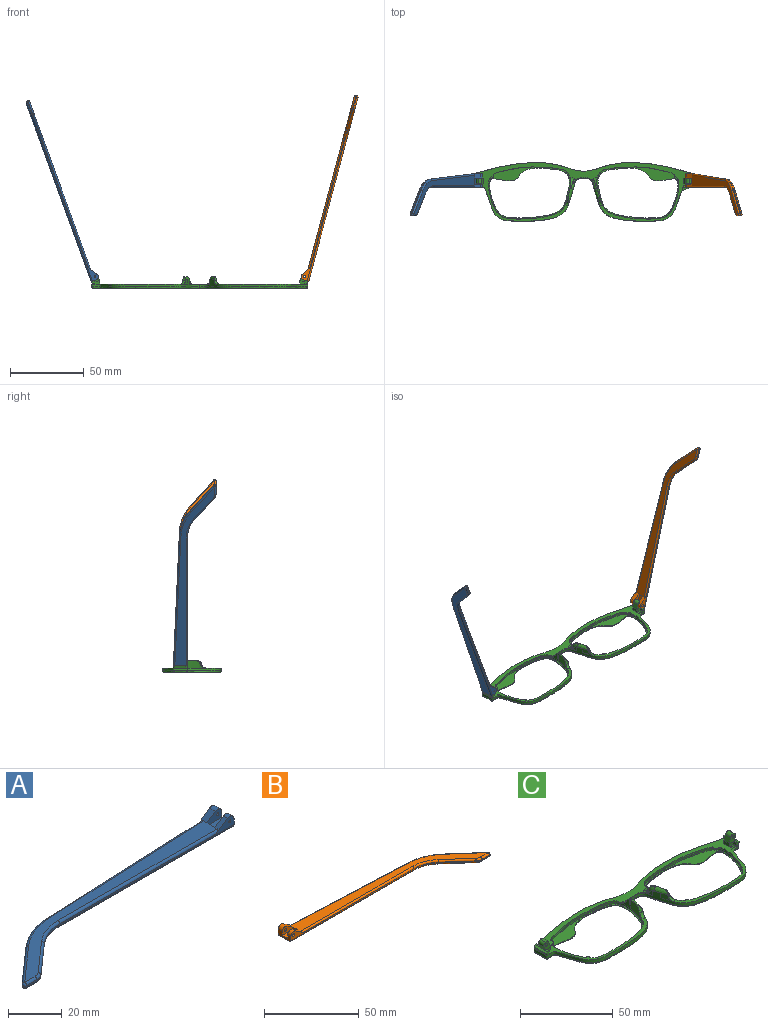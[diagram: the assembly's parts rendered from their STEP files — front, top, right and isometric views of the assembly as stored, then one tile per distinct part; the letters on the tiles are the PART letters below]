
ASSEMBLY  parts=3 mates=2
PART A: 43 faces, bbox 130.2x29.5x5.9 mm
  f0: plane 9.62x3.72mm, normal (1,0,0), area 24.7mm2, adj f1,f3,f4,f5,f10,f16,f18,f28
  f1: cylinder r=2.2mm len=3.45mm, axis (0,-1,0), area 11mm2, adj f0,f2,f4,f37
  f2: plane 6.01x3.91mm, normal (-0.55,0,0.84), area 12.7mm2, adj f1,f4,f9,f19,f37
  f3: plane 2.26x0.1mm, normal (0,0,1), area 0.1mm2, adj f0,f5,f18
  f4: plane 92.1x4.9mm, normal (0,-1,0), area 79.9mm2, adj f0,f1,f2,f14,f19,f36,f42
  f5: plane 93.42x4.13mm, normal (-0.04,1,0), area 64.8mm2, adj f0,f3,f11,f15,f17,f27,f28
  f6: plane 17.82x15.72mm, normal (-0.66,0.75,0), area 14.3mm2, adj f11,f12,f25,f30
  f7: plane 5.46x0.6mm, normal (0,-1,0), area 3.3mm2, adj f12,f13,f23,f32
  f8: plane 14.99x13.23mm, normal (0.66,-0.75,0), area 12mm2, adj f13,f14,f21,f34
  f9: plane 121.18x26.73mm, normal (0,0,1), area 627.7mm2, adj f2,f17,f19,f20,f21,f22,f23,f25
  f10: plane 129.1x27.08mm, normal (0,0,-1), area 686.5mm2, adj f0,f28,f29,f30,f32,f33,f34,f35
  f11: cylinder r=30mm len=18.52mm, axis (0,0,-1), area 12.2mm2, adj f5,f6,f26,f29
  f12: cylinder r=1mm len=1.75mm, axis (0,0,-1), area 1.5mm2, adj f6,f7,f24,f31
  f13: cylinder r=5mm len=3.31mm, axis (0,0,-1), area 2.2mm2, adj f7,f8,f22,f33
  f14: cylinder r=20mm len=13.23mm, axis (0,0,1), area 8.7mm2, adj f4,f8,f20,f35
  f15: plane 5.66x0.25mm, normal (0,0,-1), area 0.7mm2, adj f5,f17,f18
  f16: cylinder r=2.2mm len=3.45mm, axis (0,-1,0), area 14.8mm2, adj f0,f17,f18,f38
  f17: plane 6.01x3.91mm, normal (-0.55,0,0.84), area 16.9mm2, adj f5,f9,f15,f16,f18,f27,f38
  f18: plane 7.92x3.3mm, normal (0,1,0), area 15.9mm2, adj f0,f3,f15,f16,f17,f41
  f19: cylinder r=1mm len=84.18mm, axis (-1,0,0), area 131.4mm2, adj f2,f4,f9,f20
  f20: torus R=21mm, axis (0,0,1), area 23.1mm2, adj f9,f14,f19,f21
  f21: cylinder r=1mm len=15.65mm, axis (-0.75,-0.66,0), area 31.4mm2, adj f8,f9,f20,f22
  f22: torus R=4mm, axis (0,0,1), area 5.3mm2, adj f9,f13,f21,f23
  f23: cylinder r=1mm len=5.46mm, axis (-1,0,0), area 8.6mm2, adj f7,f9,f22,f24
  f24: sphere r=1mm, area 2.4mm2, adj f12,f23,f25
  f25: cylinder r=1mm len=18.48mm, axis (0.75,0.66,0), area 37.3mm2, adj f6,f9,f24,f26
  f26: torus R=29mm, axis (0,0,1), area 31.6mm2, adj f9,f11,f25,f27
  f27: cylinder r=1mm len=85.5mm, axis (1,0.04,0), area 133.5mm2, adj f5,f9,f17,f26
  f28: cylinder r=1mm len=93.46mm, axis (-1,-0.04,0), area 146.9mm2, adj f0,f5,f10,f29
  f29: torus R=29mm, axis (0,0,1), area 31.6mm2, adj f10,f11,f28,f30
  f30: cylinder r=1mm len=18.48mm, axis (-0.75,-0.66,0), area 37.3mm2, adj f6,f10,f29,f31
  f31: sphere r=1mm, area 2.4mm2, adj f12,f30,f32
  f32: cylinder r=1mm len=5.46mm, axis (1,0,0), area 8.6mm2, adj f7,f10,f31,f33
  f33: torus R=4mm, axis (0,0,1), area 5.3mm2, adj f10,f13,f32,f34
  f34: cylinder r=1mm len=15.65mm, axis (0.75,0.66,0), area 31.4mm2, adj f8,f10,f33,f35
  f35: torus R=21mm, axis (0,0,1), area 23.1mm2, adj f10,f14,f34,f36
  f36: cylinder r=1mm len=92.1mm, axis (1,0,0), area 144.7mm2, adj f0,f4,f10,f35
  f37: plane 7.92x4.7mm, normal (0,1,0), area 27mm2, adj f0,f1,f2,f39,f40,f42
  f38: plane 7.92x4.7mm, normal (0,-1,0), area 27mm2, adj f0,f16,f17,f39,f40,f41
  f39: plane 7.92x4.1mm, normal (0,0,1), area 32.5mm2, adj f0,f37,f38,f40
  f40: plane 4.1x1.4mm, normal (1,0,0), area 5.7mm2, adj f9,f37,f38,f39
  f41: cylinder r=0.5mm len=3.1mm, axis (0,-1,0), area 9.7mm2, adj f18,f38
  f42: cylinder r=0.5mm len=2.3mm, axis (0,-1,0), area 7.2mm2, adj f4,f37
PART B: 43 faces, bbox 130.2x29.5x5.9 mm
  f0: plane 9.62x3.72mm, normal (-1,0,0), area 24.7mm2, adj f1,f3,f4,f5,f10,f16,f18,f28
  f1: cylinder r=2.2mm len=3.45mm, axis (0,-1,0), area 11mm2, adj f0,f2,f4,f37
  f2: plane 6.01x3.91mm, normal (0.55,0,0.84), area 12.7mm2, adj f1,f4,f9,f19,f37
  f3: plane 2.26x0.1mm, normal (0,0,1), area 0.1mm2, adj f0,f5,f18
  f4: plane 92.1x4.9mm, normal (0,-1,0), area 78.2mm2, adj f0,f1,f2,f14,f19,f36,f42
  f5: plane 93.42x4.13mm, normal (0.04,1,0), area 64.8mm2, adj f0,f3,f11,f15,f17,f27,f28
  f6: plane 17.82x15.72mm, normal (0.66,0.75,0), area 14.3mm2, adj f11,f12,f25,f30
  f7: plane 5.46x0.6mm, normal (0,-1,0), area 3.3mm2, adj f12,f13,f23,f32
  f8: plane 14.99x13.23mm, normal (-0.66,-0.75,0), area 12mm2, adj f13,f14,f21,f34
  f9: plane 121.18x26.73mm, normal (0,0,1), area 627.7mm2, adj f2,f17,f19,f20,f21,f22,f23,f25
  f10: plane 129.1x27.08mm, normal (0,0,-1), area 686.5mm2, adj f0,f28,f29,f30,f32,f33,f34,f35
  f11: cylinder r=30mm len=18.52mm, axis (0,0,-1), area 12.2mm2, adj f5,f6,f26,f29
  f12: cylinder r=1mm len=1.75mm, axis (0,0,-1), area 1.5mm2, adj f6,f7,f24,f31
  f13: cylinder r=5mm len=3.31mm, axis (0,0,-1), area 2.2mm2, adj f7,f8,f22,f33
  f14: cylinder r=20mm len=13.23mm, axis (0,0,1), area 8.7mm2, adj f4,f8,f20,f35
  f15: plane 5.66x0.25mm, normal (0,0,-1), area 0.7mm2, adj f5,f17,f18
  f16: cylinder r=2.2mm len=3.45mm, axis (0,-1,0), area 14.8mm2, adj f0,f17,f18,f38
  f17: plane 6.01x3.91mm, normal (0.55,0,0.84), area 16.9mm2, adj f5,f9,f15,f16,f18,f27,f38
  f18: plane 7.92x3.3mm, normal (0,1,0), area 14.3mm2, adj f0,f3,f15,f16,f17,f41
  f19: cylinder r=1mm len=84.18mm, axis (1,0,0), area 131.4mm2, adj f2,f4,f9,f20
  f20: torus R=21mm, axis (0,0,1), area 23.1mm2, adj f9,f14,f19,f21
  f21: cylinder r=1mm len=15.65mm, axis (0.75,-0.66,0), area 31.4mm2, adj f8,f9,f20,f22
  f22: torus R=4mm, axis (0,0,1), area 5.3mm2, adj f9,f13,f21,f23
  f23: cylinder r=1mm len=5.46mm, axis (1,0,0), area 8.6mm2, adj f7,f9,f22,f24
  f24: sphere r=1mm, area 2.4mm2, adj f12,f23,f25
  f25: cylinder r=1mm len=18.48mm, axis (-0.75,0.66,0), area 37.3mm2, adj f6,f9,f24,f26
  f26: torus R=29mm, axis (0,0,1), area 31.6mm2, adj f9,f11,f25,f27
  f27: cylinder r=1mm len=85.5mm, axis (-1,0.04,0), area 133.5mm2, adj f5,f9,f17,f26
  f28: cylinder r=1mm len=93.46mm, axis (1,-0.04,0), area 146.9mm2, adj f0,f5,f10,f29
  f29: torus R=29mm, axis (0,0,1), area 31.6mm2, adj f10,f11,f28,f30
  f30: cylinder r=1mm len=18.48mm, axis (0.75,-0.66,0), area 37.3mm2, adj f6,f10,f29,f31
  f31: sphere r=1mm, area 2.4mm2, adj f12,f30,f32
  f32: cylinder r=1mm len=5.46mm, axis (-1,0,0), area 8.6mm2, adj f7,f10,f31,f33
  f33: torus R=4mm, axis (0,0,1), area 5.3mm2, adj f10,f13,f32,f34
  f34: cylinder r=1mm len=15.65mm, axis (-0.75,0.66,0), area 31.4mm2, adj f8,f10,f33,f35
  f35: torus R=21mm, axis (0,0,1), area 23.1mm2, adj f10,f14,f34,f36
  f36: cylinder r=1mm len=92.1mm, axis (-1,0,0), area 144.7mm2, adj f0,f4,f10,f35
  f37: plane 7.92x4.7mm, normal (0,1,0), area 25.4mm2, adj f0,f1,f2,f39,f40,f42
  f38: plane 7.92x4.7mm, normal (0,-1,0), area 25.4mm2, adj f0,f16,f17,f39,f40,f41
  f39: plane 7.92x4.1mm, normal (0,0,1), area 32.5mm2, adj f0,f37,f38,f40
  f40: plane 4.1x1.4mm, normal (-1,0,0), area 5.7mm2, adj f9,f37,f38,f39
  f41: cylinder r=0.88mm len=3.1mm, axis (0,-1,0), area 17mm2, adj f18,f38
  f42: cylinder r=0.88mm len=2.3mm, axis (0,-1,0), area 12.6mm2, adj f4,f37
PART C: 118 faces, bbox 148.1x40.9x17.9 mm
  f0: bspline ~1.82x1.22mm, area 0.7mm2, adj f2,f7,f37,f52
  f1: plane 147.69x40.46mm, normal (0,0,1), area 858.2mm2, adj f4,f5,f6,f7,f8,f12,f20,f23
  f2: bspline ~6.1x4.93mm, area 12.7mm2, adj f0,f7,f37,f41,f43,f52,f53
  f3: plane 4.46x1.45mm, normal (0,0,1), area 0.1mm2, adj f7,f38
  f4: plane 1.23x0.04mm, normal (0,0,1), area 0mm2, adj f1,f7,f22
  f5: plane 6.97x5.07mm, normal (0,1,0), area 22.7mm2, adj f1,f20,f21,f25,f27,f28,f30,f31
  f6: plane 3.2x2.36mm, normal (0,-1,0), area 5.7mm2, adj f1,f20,f26,f29
  f7: extruded ~73.26x39.84mm, area 292.7mm2, adj f0,f1,f2,f3,f4,f8,f13,f14
  f8: extruded ~35.39x5.69mm, area 72.2mm2, adj f1,f7,f18,f67
  f9: plane 144.78x37.85mm, normal (0,0,-1), area 782.7mm2, adj f13,f15,f17,f18,f19,f71,f73,f75
  f10: plane 56.06x35.45mm, normal (0,0,1), area 232.2mm2, adj f11,f19
  f11: extruded ~55.69x35.36mm, area 160.5mm2, adj f10,f12
  f12: extruded ~55.69x35.36mm, area 226.3mm2, adj f1,f11,f39,f40,f41,f42,f43,f44
  f13: bspline ~73.27x30.39mm, area 161.7mm2, adj f7,f9,f14,f71
  f14: bspline ~1x1mm, area 0.8mm2, adj f7,f13,f15
  f15: bspline ~8.99x1.23mm, area 12.6mm2, adj f7,f9,f14,f16
  f16: bspline ~1.04x1mm, area 0.7mm2, adj f7,f15,f17
  f17: bspline ~45.86x8.59mm, area 59.8mm2, adj f7,f9,f16,f18
  f18: bspline ~37.01x6.7mm, area 56.6mm2, adj f8,f9,f17,f76
  f19: bspline ~56.18x36.02mm, area 237.5mm2, adj f9,f10
  f20: plane 4x2.36mm, normal (-1,0,0), area 9.5mm2, adj f1,f5,f6,f21
  f21: plane 4x0.02mm, normal (0.34,0,0.94), area 0.1mm2, adj f5,f20,f28
  f22: plane 2.76x2.53mm, normal (0,-1,0), area 3.9mm2, adj f4,f26,f27,f35,f56
  f23: plane 7.67x1.6mm, normal (0.94,0,-0.34), area 13mm2, adj f1,f35,f36,f56
  f24: plane 2.1x1.69mm, normal (0,1,0), area 2.8mm2, adj f1,f25,f27,f36,f56
  f25: plane 3.3x2.1mm, normal (-1,0,0), area 6.9mm2, adj f1,f5,f24,f27
  f26: plane 2.35x2.1mm, normal (-1,0,0), area 4.9mm2, adj f1,f6,f22,f27,f29
  f27: plane 9.65x1.24mm, normal (0,0,1), area 8.2mm2, adj f5,f22,f24,f25,f26,f29,f30,f56
  f28: plane 4x3.31mm, normal (-0.94,0,0.34), area 14.1mm2, adj f5,f21,f29,f32
  f29: plane 5.77x5.06mm, normal (0,-1,0), area 17mm2, adj f6,f26,f27,f28,f30,f31,f32,f33
  f30: plane 4x2.21mm, normal (0.94,0,-0.34), area 9.4mm2, adj f5,f27,f29,f33
  f31: plane 4x0.01mm, normal (0.34,0,0.94), area 0mm2, adj f5,f29,f32,f33
  f32: cylinder r=1.98mm len=4mm, axis (0,1,0), area 12.4mm2, adj f5,f28,f29,f31
  f33: cylinder r=1.98mm len=4mm, axis (0,-1,0), area 12.4mm2, adj f5,f29,f30,f31
  f34: cylinder r=0.88mm len=4mm, axis (0,-1,0), area 22mm2, adj f5,f29
  f35: cone r=1mm half-angle=20deg, axis (0,0,1), area 2.3mm2, adj f1,f22,f23,f56
  f36: cylinder r=1mm len=2.28mm, axis (-0.34,0,-0.94), area 3mm2, adj f1,f23,f24,f56
  f37: extruded ~3.67x3.11mm, area 5.9mm2, adj f0,f2,f7,f59
  f38: extruded ~4.44x3.32mm, area 15.1mm2, adj f3,f7,f42,f43,f55
  f39: extruded ~4.98x1.37mm, area 6.6mm2, adj f12,f41
  f40: plane 3.63x0.97mm, normal (0,0,1), area 0.3mm2, adj f12,f41,f43
  f41: bspline ~15.5x15.35mm, area 6.4mm2, adj f2,f12,f39,f40,f54
  f42: bspline ~7.26x7.26mm, area 6.3mm2, adj f12,f38,f43,f55
  f43: bspline ~10.29x4.84mm, area 21.4mm2, adj f2,f7,f12,f38,f40,f42
  f44: plane 3.19x1.37mm, normal (0,0,-1), area 2.1mm2, adj f12,f45
  f45: cylinder r=2.28mm len=3.17mm, axis (0,0,1), area 2.1mm2, adj f1,f12,f44,f54
  f46: plane 3.14x2.79mm, normal (0,0,-1), area 3.9mm2, adj f12,f47
  f47: cylinder r=2.28mm len=3.13mm, axis (0,0,1), area 2.5mm2, adj f1,f12,f46
  f48: plane 1.79x1.31mm, normal (0,0,-1), area 0.9mm2, adj f12,f49
  f49: cylinder r=1.3mm len=1.78mm, axis (0,0,1), area 1.3mm2, adj f1,f12,f48
  f50: plane 1.95x1.68mm, normal (0,0,-1), area 1.5mm2, adj f12,f51
  f51: cylinder r=1.3mm len=1.93mm, axis (0,0,1), area 1.5mm2, adj f1,f12,f50
  f52: bspline ~2.66x2.04mm, area 1.9mm2, adj f0,f2,f7,f53,f58
  f53: bspline ~3.55x3.47mm, area 3.7mm2, adj f1,f2,f52,f54,f58
  f54: bspline ~6.16x4.45mm, area 7.9mm2, adj f1,f12,f41,f45,f53
  f55: bspline ~3.7x3.66mm, area 7.8mm2, adj f1,f7,f12,f38,f42
  f56: plane 9.71x1.44mm, normal (0.34,0,0.94), area 13.9mm2, adj f22,f23,f24,f27,f35,f36
  f57: bspline ~6.38x2.14mm, area 2.6mm2, adj f1,f7,f58,f115
  f58: bspline ~2.1x1.46mm, area 0.6mm2, adj f7,f52,f53,f57
  f59: bspline ~5.24x1.75mm, area 0mm2, adj f7,f37
  f60: bspline ~2.19x1.4mm, area 0.7mm2, adj f61,f66,f95,f110
  f61: bspline ~6.1x4.93mm, area 12.6mm2, adj f60,f66,f95,f99,f101,f110,f111
  f62: plane 4.46x1.45mm, normal (0,0,1), area 0.1mm2, adj f66,f96
  f63: plane 1.23x0.04mm, normal (0,0,1), area 0mm2, adj f1,f66,f80
  f64: plane 6.97x5.07mm, normal (0,1,0), area 22.7mm2, adj f1,f78,f79,f83,f85,f86,f88,f89
  f65: plane 3.2x2.36mm, normal (0,-1,0), area 5.7mm2, adj f1,f78,f84,f87
  f66: extruded ~73.26x39.84mm, area 292.7mm2, adj f1,f7,f60,f61,f62,f63,f67,f71
  f67: extruded ~35.39x5.69mm, area 72.2mm2, adj f1,f8,f66,f76
  f68: plane 56.06x35.45mm, normal (0,0,1), area 232.2mm2, adj f69,f77
  f69: extruded ~55.69x35.36mm, area 160.5mm2, adj f68,f70
  f70: extruded ~55.69x35.36mm, area 226.4mm2, adj f1,f69,f97,f98,f99,f100,f101,f102
  f71: bspline ~73.83x30.39mm, area 161.7mm2, adj f9,f13,f66,f72
  f72: bspline ~1x1mm, area 0.8mm2, adj f66,f71,f73
  f73: bspline ~8.99x1.23mm, area 12.6mm2, adj f9,f66,f72,f74
  f74: bspline ~1.04x1mm, area 0.8mm2, adj f66,f73,f75
  f75: bspline ~45.86x8.59mm, area 59.8mm2, adj f9,f66,f74,f76
  f76: bspline ~37.01x6.7mm, area 56.6mm2, adj f9,f18,f67,f75
  f77: bspline ~56.18x36.02mm, area 237.5mm2, adj f9,f68
  f78: plane 4x2.36mm, normal (1,0,0), area 9.5mm2, adj f1,f64,f65,f79
  f79: plane 4x0.02mm, normal (-0.34,0,0.94), area 0.1mm2, adj f64,f78,f86
  f80: plane 2.76x2.53mm, normal (0,-1,0), area 3.9mm2, adj f63,f84,f85,f93,f114
  f81: plane 7.67x1.6mm, normal (-0.94,0,-0.34), area 13mm2, adj f1,f93,f94,f114
  f82: plane 2.1x1.69mm, normal (0,1,0), area 2.8mm2, adj f1,f83,f85,f94,f114
  f83: plane 3.3x2.1mm, normal (1,0,0), area 6.9mm2, adj f1,f64,f82,f85
  f84: plane 2.35x2.1mm, normal (1,0,0), area 4.9mm2, adj f1,f65,f80,f85,f87
  f85: plane 9.65x1.24mm, normal (0,0,1), area 8.2mm2, adj f64,f80,f82,f83,f84,f87,f88,f114
  f86: plane 4x3.31mm, normal (0.94,0,0.34), area 14.1mm2, adj f64,f79,f87,f90
  f87: plane 5.77x5.06mm, normal (0,-1,0), area 17mm2, adj f65,f84,f85,f86,f88,f89,f90,f91
  f88: plane 4x2.21mm, normal (-0.94,0,-0.34), area 9.4mm2, adj f64,f85,f87,f91
  f89: plane 4x0.01mm, normal (-0.34,0,0.94), area 0mm2, adj f64,f87,f90,f91
  f90: cylinder r=1.98mm len=4mm, axis (0,1,0), area 12.4mm2, adj f64,f86,f87,f89
  f91: cylinder r=1.98mm len=4mm, axis (0,-1,0), area 12.4mm2, adj f64,f87,f88,f89
  f92: cylinder r=0.88mm len=4mm, axis (0,-1,0), area 22mm2, adj f64,f87
  f93: cone r=1mm half-angle=20deg, axis (0,0,1), area 2.3mm2, adj f1,f80,f81,f114
  f94: cylinder r=1mm len=2.28mm, axis (0.34,0,-0.94), area 3mm2, adj f1,f81,f82,f114
  f95: extruded ~3.67x3.11mm, area 5.9mm2, adj f60,f61,f66,f117
  f96: extruded ~4.44x3.32mm, area 15.1mm2, adj f62,f66,f100,f101,f113
  f97: extruded ~4.98x1.36mm, area 6.6mm2, adj f70,f99
  f98: plane 3.63x0.97mm, normal (0,0,1), area 0.3mm2, adj f70,f99,f101
  f99: bspline ~15.5x15.35mm, area 6.4mm2, adj f61,f70,f97,f98,f112
  f100: bspline ~7.26x7.26mm, area 6.2mm2, adj f70,f96,f101,f113
  f101: bspline ~10.29x4.84mm, area 21.5mm2, adj f61,f66,f70,f96,f98,f100
  f102: plane 3.19x1.37mm, normal (0,0,-1), area 2.1mm2, adj f70,f103
  f103: cylinder r=2.28mm len=3.17mm, axis (0,0,1), area 2.1mm2, adj f1,f70,f102,f112
  f104: plane 3.14x2.79mm, normal (0,0,-1), area 3.9mm2, adj f70,f105
  f105: cylinder r=2.28mm len=3.13mm, axis (0,0,1), area 2.5mm2, adj f1,f70,f104
  f106: plane 1.79x1.31mm, normal (0,0,-1), area 0.9mm2, adj f70,f107
  f107: cylinder r=1.3mm len=1.78mm, axis (0,0,1), area 1.3mm2, adj f1,f70,f106
  f108: plane 1.95x1.68mm, normal (0,0,-1), area 1.5mm2, adj f70,f109
  f109: cylinder r=1.3mm len=1.93mm, axis (0,0,1), area 1.5mm2, adj f1,f70,f108
  f110: bspline ~2.65x2.03mm, area 1.9mm2, adj f60,f61,f66,f111,f116
  f111: bspline ~3.55x3.47mm, area 3.7mm2, adj f1,f61,f110,f112,f116
  f112: bspline ~5.94x4.42mm, area 7.9mm2, adj f1,f70,f99,f103,f111
  f113: bspline ~3.7x3.66mm, area 7.8mm2, adj f1,f66,f70,f96,f100
  f114: plane 9.71x1.44mm, normal (-0.34,0,0.94), area 13.9mm2, adj f80,f81,f82,f85,f93,f94
  f115: bspline ~6.38x2.14mm, area 2.6mm2, adj f1,f57,f66,f116
  f116: bspline ~2.1x1.46mm, area 0.6mm2, adj f66,f110,f111,f115
  f117: bspline ~5.24x1.75mm, area 0mm2, adj f66,f95
PLACE A rot(axis=(0,1,0),70deg) t=(-84.77,-5.75,56)mm
PLACE B rot(axis=(0,-1,0),75deg) t=(68.2,-5.75,-61.61)mm
PLACE C t=(10.15,-1.13,-5.77)mm
MATE revolute A.f1 <-> C.f90  axis (0,-1,0) through (-60.89,2.72,1.22)mm
MATE revolute B.f41 <-> C.f33  axis (0,-1,0) through (81.2,2.72,1.21)mm
